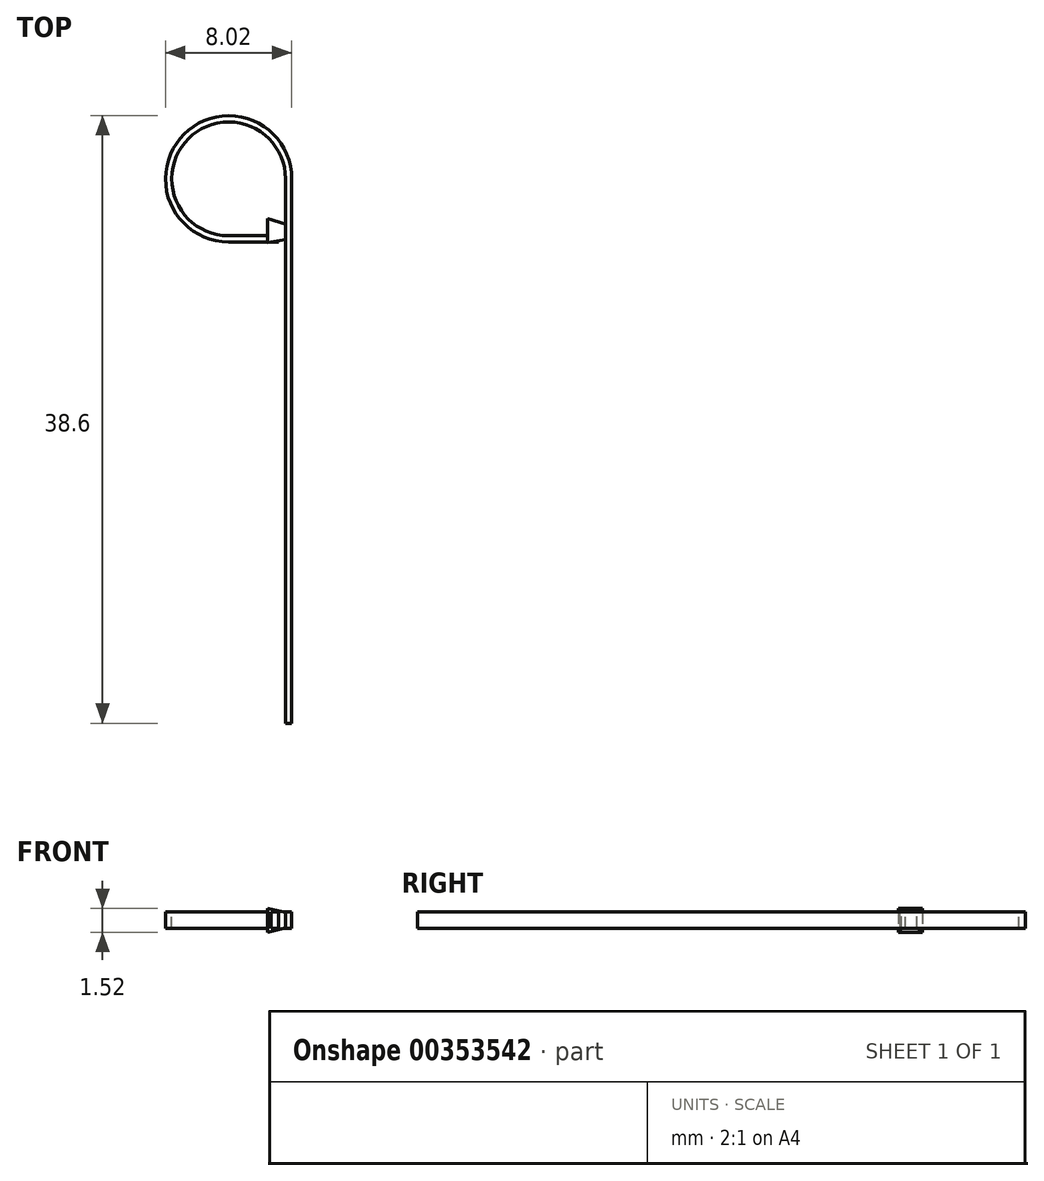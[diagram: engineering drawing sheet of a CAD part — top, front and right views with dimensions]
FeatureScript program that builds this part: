
annotation { "Feature Type Name" : "Feature", "Feature Type Description" : "" }
export const myFeature = defineFeature(function(context is Context, id is Id, definition is map)
    precondition{}
    {
        {
            var Q0;
            Q0=qCreatedBy(makeId("Top.planeOp"),FACE);
            var sketch = newSketch(context, id + "F0", { "sketchPlane" : qUnion([Q0])});
            skLineSegment(sketch, "E0", {"start": v(0, -25.4) * mm, "end": v(0, 9.19) * mm});
            skLineSegment(sketch, "E1", {"start": v(-0.65, 5.38) * mm, "end": v(-3.82, 5.38) * mm});
            skArc(sketch, "E2", {"start": v(0, 9.19) * mm, "mid": v(-6.5, 11.89) * mm, "end": v(-3.82, 5.38) * mm});
            skSolve(sketch);
        }
        {
            var Q0;
            Q0=qCreatedBy(makeId("Front.planeOp"),FACE);
            cPlane(context, id + "F1", {"entities" : qUnion([Q0]), "cplaneType" : CPlaneType.OFFSET, "offset" : 25.4 * mm, "width" : 152.4 * mm, "height" : 152.4 * mm});
        }
        {
            var Q0;
            Q0=qCreatedBy(id+"F1.planeOp",FACE);
            var sketch = newSketch(context, id + "F2", { "sketchPlane" : qUnion([Q0])});
            skLineSegment(sketch, "E3.bottom", {"start": v(0.2, -0.53) * mm, "end": v(-0.2, -0.53) * mm});
            skLineSegment(sketch, "E3.top", {"start": v(0.2, 0.53) * mm, "end": v(-0.2, 0.53) * mm});
            skLineSegment(sketch, "E3.left", {"start": v(0.2, -0.53) * mm, "end": v(0.2, 0.53) * mm});
            skLineSegment(sketch, "E3.right", {"start": v(-0.2, -0.53) * mm, "end": v(-0.2, 0.53) * mm});
            skPoint(sketch, "E3.middle", {"position": v(0, 0) * mm});
            skSolve(sketch);
        }
        {
            var Q0;
            Q0=qCreatedBy(makeId("Right.planeOp"),FACE);
            cPlane(context, id + "F3", {"entities" : qUnion([Q0]), "cplaneType" : CPlaneType.OFFSET, "offset" : 0.2 * mm, "width" : 152.4 * mm, "height" : 152.4 * mm});
        }
        {
            var Q0;
            Q0=qCreatedBy(makeId("Right.planeOp"),FACE);
            cPlane(context, id + "F4", {"entities" : qUnion([Q0]), "cplaneType" : CPlaneType.OFFSET, "offset" : 1.35 * mm, "oppositeDirection" : true, "width" : 152.4 * mm, "height" : 152.4 * mm});
        }
        {
            var Q0;
            Q0=qCreatedBy(id+"F3.planeOp",FACE);
            var sketch = newSketch(context, id + "F5", { "sketchPlane" : qUnion([Q0])});
            skLineSegment(sketch, "E4.bottom", {"start": v(5.38, 0.4) * mm, "end": v(6.17, 0.4) * mm});
            skLineSegment(sketch, "E4.top", {"start": v(5.38, -0.4) * mm, "end": v(6.17, -0.4) * mm});
            skLineSegment(sketch, "E4.left", {"start": v(5.38, 0.4) * mm, "end": v(5.38, -0.4) * mm});
            skLineSegment(sketch, "E4.right", {"start": v(6.17, 0.4) * mm, "end": v(6.17, -0.4) * mm});
            skPoint(sketch, "E4.middle", {"position": v(5.77, 0) * mm});
            skSolve(sketch);
        }
        {
            var Q0;
            Q0=qCreatedBy(id+"F4.planeOp",FACE);
            var sketch = newSketch(context, id + "F6", { "sketchPlane" : qUnion([Q0])});
            skLineSegment(sketch, "E5.bottom", {"start": v(6.67, 0.76) * mm, "end": v(5.14, 0.76) * mm});
            skLineSegment(sketch, "E5.top", {"start": v(6.67, -0.76) * mm, "end": v(5.14, -0.76) * mm});
            skLineSegment(sketch, "E5.left", {"start": v(6.67, 0.76) * mm, "end": v(6.67, -0.76) * mm});
            skLineSegment(sketch, "E5.right", {"start": v(5.14, 0.76) * mm, "end": v(5.14, -0.76) * mm});
            skPoint(sketch, "E5.middle", {"position": v(5.9, 0) * mm});
            skSolve(sketch);
        }
        {
            var Q1;
            Q1 = qSketchRegion(id + "F5", true);
            var Q2;
            Q2 = qSketchRegion(id + "F6", true);
            loft(context, id + "F7", {"sheetProfilesArray" : [{ "sheetProfileEntities" : qUnion([Q1]) }, { "sheetProfileEntities" : qUnion([Q2]) }]});
        }
        {
            var Q0;
            Q0 = qSketchRegion(id + "F2", true);
            var Q1;
            Q1 = qConstructionFilter(qBodyType(qCreatedBy(id + "F0" ,EDGE), BodyType.WIRE), ConstructionObject.NO);
            sweep(context, id + "F8", {"operationType" : NewBodyOperationType.ADD, "profiles" : qUnion([Q0]), "path" : qUnion([Q1])});
        }
    });
